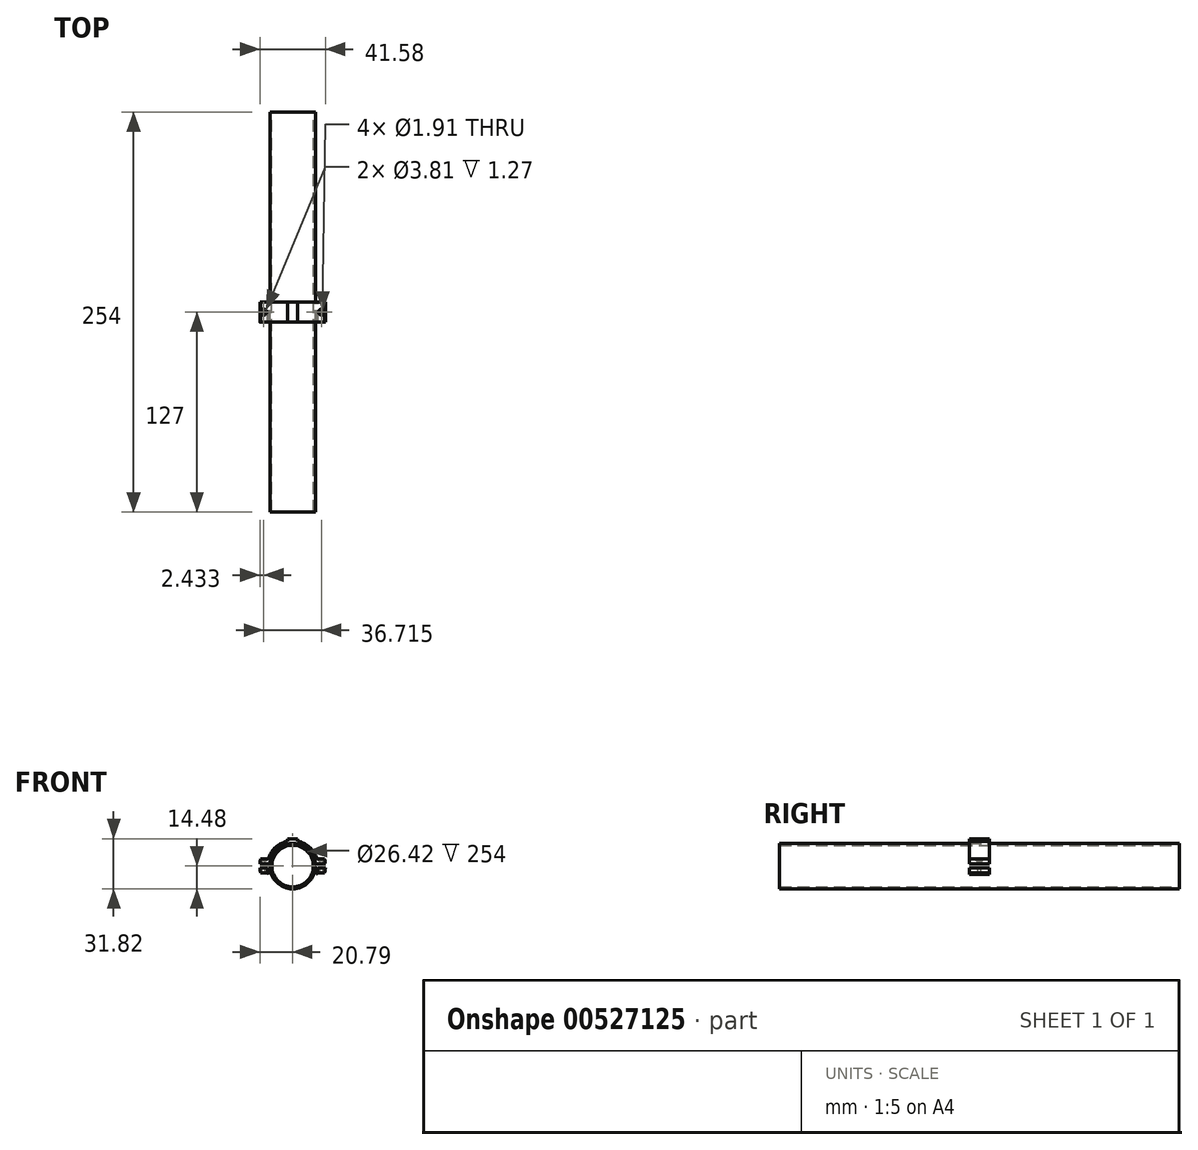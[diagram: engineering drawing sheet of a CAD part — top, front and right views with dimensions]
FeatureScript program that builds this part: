
annotation { "Feature Type Name" : "Feature", "Feature Type Description" : "" }
export const myFeature = defineFeature(function(context is Context, id is Id, definition is map)
    precondition{}
    {
        {
            var Q0;
            Q0=qCreatedBy(makeId("Front.planeOp"),FACE);
            var sketch = newSketch(context, id + "F0", { "sketchPlane" : qUnion([Q0])});
            skCircle(sketch, "E0", {"center": v(0, 0) * mm, "radius": 14.48 * mm});
            skCircle(sketch, "E1.0", {"center": v(0, 0) * mm, "radius": 13.2 * mm});
            skCircle(sketch, "E2", {"center": v(0, 0) * mm, "radius": 20.83 * mm});
            skCircle(sketch, "E3", {"center": v(0, 0) * mm, "radius": 16.07 * mm});
            skLineSegment(sketch, "E4.bottom", {"start": v(15.44, 4.45) * mm, "end": v(20.79, 4.45) * mm});
            skLineSegment(sketch, "E4.top", {"start": v(15.44, 1.27) * mm, "end": v(20.79, 1.27) * mm});
            skLineSegment(sketch, "E4.left", {"start": v(15.44, 4.45) * mm, "end": v(15.44, 1.27) * mm});
            skLineSegment(sketch, "E4.right", {"start": v(20.79, 4.45) * mm, "end": v(20.79, 1.27) * mm});
            skLineSegment(sketch, "E5", {"start": v(15.44, 1.27) * mm, "end": v(15.44, -4.45) * mm});
            skLineSegment(sketch, "E6.bottom", {"start": v(15.44, -4.45) * mm, "end": v(20.79, -4.45) * mm});
            skLineSegment(sketch, "E6.top", {"start": v(15.44, -1.27) * mm, "end": v(20.79, -1.27) * mm});
            skLineSegment(sketch, "E6.left", {"start": v(15.44, -4.45) * mm, "end": v(15.44, -1.27) * mm});
            skLineSegment(sketch, "E6.right", {"start": v(20.79, -4.45) * mm, "end": v(20.79, -1.27) * mm});
            skLineSegment(sketch, "E7.MirrorCS", {"start": v(-15.44, 4.45) * mm, "end": v(-20.79, 4.45) * mm});
            skLineSegment(sketch, "E8.MirrorCS", {"start": v(-20.79, 4.45) * mm, "end": v(-20.79, 1.27) * mm});
            skLineSegment(sketch, "E9.MirrorCS", {"start": v(-15.44, 1.27) * mm, "end": v(-20.79, 1.27) * mm});
            skLineSegment(sketch, "E10.MirrorCS", {"start": v(-15.44, 4.45) * mm, "end": v(-15.44, 1.27) * mm});
            skLineSegment(sketch, "E11.MirrorCS", {"start": v(-15.44, 1.27) * mm, "end": v(-15.44, -4.45) * mm});
            skLineSegment(sketch, "E12.MirrorCS", {"start": v(-15.44, -1.27) * mm, "end": v(-20.79, -1.27) * mm});
            skLineSegment(sketch, "E13.MirrorCS", {"start": v(-20.79, -4.45) * mm, "end": v(-20.79, -1.27) * mm});
            skLineSegment(sketch, "E14.MirrorCS", {"start": v(-15.44, -4.45) * mm, "end": v(-20.79, -4.45) * mm});
            skLineSegment(sketch, "E15.MirrorCS", {"start": v(-15.44, -4.45) * mm, "end": v(-15.44, -1.27) * mm});
            skLineSegment(sketch, "E16", {"start": v(-15.44, 1.27) * mm, "end": v(-14.42, 1.27) * mm});
            skLineSegment(sketch, "E17", {"start": v(-15.44, -1.27) * mm, "end": v(-14.42, -1.27) * mm});
            skLineSegment(sketch, "E18", {"start": v(15.44, 1.27) * mm, "end": v(14.42, 1.27) * mm});
            skCircle(sketch, "E19", {"center": v(16.37, -5.72) * mm, "radius": 1.27 * mm});
            skCircle(sketch, "E20", {"center": v(16.37, 5.72) * mm, "radius": 1.27 * mm});
            skCircle(sketch, "E21", {"center": v(-16.37, 5.72) * mm, "radius": 1.27 * mm});
            skCircle(sketch, "E22", {"center": v(-16.37, -5.72) * mm, "radius": 1.27 * mm});
            skLineSegment(sketch, "E23", {"start": v(15.44, -1.27) * mm, "end": v(14.42, -1.27) * mm});
            skLineSegment(sketch, "E24.bottom", {"start": v(-3.18, 17.34) * mm, "end": v(3.17, 17.34) * mm});
            skLineSegment(sketch, "E24.top", {"start": v(-3.18, 14.8) * mm, "end": v(3.17, 14.8) * mm});
            skLineSegment(sketch, "E24.left", {"start": v(-3.18, 17.34) * mm, "end": v(-3.18, 14.8) * mm});
            skLineSegment(sketch, "E24.right", {"start": v(3.18, 17.34) * mm, "end": v(3.17, 14.8) * mm});
            skPoint(sketch, "E24.middle", {"position": v(0, 16.07) * mm});
            skSolve(sketch);
        }
        {
            var Q0;
            Q0=makeQuery(id+"F0.imprint","IMPRINT",FACE,{"disambiguationData":[TD([[makeQuery(id+"F0.imprint","IMPRINT",EDGE,{"derivedFrom":sQuery(id+"F0.wireOp",EDGE,"E0")}),1.0]])]});
            extrude(context, id + "F1", {"entities" : qUnion([Q0]), "depth" : 254 * mm, "offsetDistance" : 25.4 * mm, "symmetric" : true});
        }
        {
            var Q0;
            {var subQ0=sQuery(id+"F0.wireOp",EDGE,"E7.MirrorCS");var subQ1=sQuery(id+"F0.wireOp",EDGE,"E2");var subQ2=makeQuery(id+"F0.imprint","INTERSECT",VERTEX,{"derivedFrom":[subQ1,subQ0]});Q0=makeQuery(id+"F0.imprint","IMPRINT",FACE,{"disambiguationData":[TD([[makeQuery(id+"F0.imprint","IMPRINT",EDGE,{"disambiguationData":[TD([[subQ2,1.0]])],"derivedFrom":subQ0}),1.0]])]});}
            var Q1;
            {var subQ0=sQuery(id+"F0.wireOp",EDGE,"E10.MirrorCS");Q1=makeQuery(id+"F0.imprint","IMPRINT",FACE,{"disambiguationData":[TD([[makeQuery(id+"F0.imprint","IMPRINT",EDGE,{"derivedFrom":subQ0}),-1.0]])]});}
            var Q2;
            {var subQ1=sQuery(id+"F0.wireOp",EDGE,"E3");var subQ3=sQuery(id+"F0.wireOp",EDGE,"E21");var subQ4=makeQuery(id+"F0.imprint","INTERSECT",VERTEX,{"derivedFrom":[subQ1,subQ3]});Q2=makeQuery(id+"F0.imprint","IMPRINT",FACE,{"disambiguationData":[TD([[makeQuery(id+"F0.imprint","IMPRINT",EDGE,{"disambiguationData":[TD([[subQ4,1.0]])],"derivedFrom":subQ3}),-1.0]])]});}
            var Q3;
            {var subQ3=sQuery(id+"F0.wireOp",EDGE,"E4.left");Q3=makeQuery(id+"F0.imprint","IMPRINT",FACE,{"disambiguationData":[TD([[makeQuery(id+"F0.imprint","IMPRINT",EDGE,{"derivedFrom":subQ3}),-1.0]])]});}
            var Q4;
            {var subQ0=sQuery(id+"F0.wireOp",EDGE,"E15.MirrorCS");Q4=makeQuery(id+"F0.imprint","IMPRINT",FACE,{"disambiguationData":[TD([[makeQuery(id+"F0.imprint","IMPRINT",EDGE,{"derivedFrom":subQ0}),1.0]])]});}
            var Q5;
            {var subQ0=sQuery(id+"F0.wireOp",EDGE,"E14.MirrorCS");var subQ5=sQuery(id+"F0.wireOp",EDGE,"E2");var subQ8=makeQuery(id+"F0.imprint","INTERSECT",VERTEX,{"derivedFrom":[subQ5,subQ0]});Q5=makeQuery(id+"F0.imprint","IMPRINT",FACE,{"disambiguationData":[TD([[makeQuery(id+"F0.imprint","IMPRINT",EDGE,{"disambiguationData":[TD([[subQ8,1.0]])],"derivedFrom":subQ0}),-1.0]])]});}
            var Q6;
            {var subQ1=sQuery(id+"F0.wireOp",EDGE,"E3");var subQ3=sQuery(id+"F0.wireOp",EDGE,"E22");var subQ4=makeQuery(id+"F0.imprint","INTERSECT",VERTEX,{"derivedFrom":[subQ1,subQ3]});Q6=makeQuery(id+"F0.imprint","IMPRINT",FACE,{"disambiguationData":[TD([[makeQuery(id+"F0.imprint","IMPRINT",EDGE,{"disambiguationData":[TD([[subQ4,-1.0]])],"derivedFrom":subQ3}),-1.0]])]});}
            var Q7;
            {var subQ1=sQuery(id+"F0.wireOp",EDGE,"E3");var subQ3=sQuery(id+"F0.wireOp",EDGE,"E19");var subQ4=makeQuery(id+"F0.imprint","INTERSECT",VERTEX,{"derivedFrom":[subQ1,subQ3]});Q7=makeQuery(id+"F0.imprint","IMPRINT",FACE,{"disambiguationData":[TD([[makeQuery(id+"F0.imprint","IMPRINT",EDGE,{"disambiguationData":[TD([[subQ4,1.0]])],"derivedFrom":subQ3}),-1.0]])]});}
            var Q8;
            {var subQ0=sQuery(id+"F0.wireOp",EDGE,"E6.left");Q8=makeQuery(id+"F0.imprint","IMPRINT",FACE,{"disambiguationData":[TD([[makeQuery(id+"F0.imprint","IMPRINT",EDGE,{"derivedFrom":subQ0}),-1.0]])]});}
            var Q9;
            {var subQ0=sQuery(id+"F0.wireOp",EDGE,"E6.bottom");var subQ1=sQuery(id+"F0.wireOp",EDGE,"E2");var subQ2=makeQuery(id+"F0.imprint","INTERSECT",VERTEX,{"derivedFrom":[subQ1,subQ0]});Q9=makeQuery(id+"F0.imprint","IMPRINT",FACE,{"disambiguationData":[TD([[makeQuery(id+"F0.imprint","IMPRINT",EDGE,{"disambiguationData":[TD([[subQ2,1.0]])],"derivedFrom":subQ0}),1.0]])]});}
            var Q10;
            {var subQ0=sQuery(id+"F0.wireOp",EDGE,"E4.left");Q10=makeQuery(id+"F0.imprint","IMPRINT",FACE,{"disambiguationData":[TD([[makeQuery(id+"F0.imprint","IMPRINT",EDGE,{"derivedFrom":subQ0}),1.0]])]});}
            var Q11;
            {var subQ0=sQuery(id+"F0.wireOp",EDGE,"E4.bottom");var subQ1=sQuery(id+"F0.wireOp",EDGE,"E2");var subQ2=makeQuery(id+"F0.imprint","INTERSECT",VERTEX,{"derivedFrom":[subQ1,subQ0]});Q11=makeQuery(id+"F0.imprint","IMPRINT",FACE,{"disambiguationData":[TD([[makeQuery(id+"F0.imprint","IMPRINT",EDGE,{"disambiguationData":[TD([[subQ2,1.0]])],"derivedFrom":subQ0}),-1.0]])]});}
            var Q12;
            {var subQ1=sQuery(id+"F0.wireOp",EDGE,"E3");var subQ3=sQuery(id+"F0.wireOp",EDGE,"E20");var subQ4=makeQuery(id+"F0.imprint","INTERSECT",VERTEX,{"derivedFrom":[subQ1,subQ3]});Q12=makeQuery(id+"F0.imprint","IMPRINT",FACE,{"disambiguationData":[TD([[makeQuery(id+"F0.imprint","IMPRINT",EDGE,{"disambiguationData":[TD([[subQ4,-1.0]])],"derivedFrom":subQ3}),-1.0]])]});}
            var Q13;
            {var subQ4=sQuery(id+"F0.wireOp",EDGE,"E6.left");Q13=makeQuery(id+"F0.imprint","IMPRINT",FACE,{"disambiguationData":[TD([[makeQuery(id+"F0.imprint","IMPRINT",EDGE,{"derivedFrom":subQ4}),1.0]])]});}
            var Q14;
            {var subQ5=sQuery(id+"F0.wireOp",EDGE,"E24.top");Q14=makeQuery(id+"F0.imprint","IMPRINT",FACE,{"disambiguationData":[TD([[makeQuery(id+"F0.imprint","IMPRINT",EDGE,{"derivedFrom":subQ5}),1.0]])]});}
            var Q15;
            {var subQ5=sQuery(id+"F0.wireOp",EDGE,"E24.bottom");Q15=makeQuery(id+"F0.imprint","IMPRINT",FACE,{"disambiguationData":[TD([[makeQuery(id+"F0.imprint","IMPRINT",EDGE,{"derivedFrom":subQ5}),-1.0]])]});}
            extrude(context, id + "F2", {"entities" : qUnion([Q0, Q1, Q2, Q3, Q4, Q5, Q6, Q7, Q8, Q9, Q10, Q11, Q12, Q13, Q14, Q15]), "depth" : 12.7 * mm, "offsetDistance" : 25.4 * mm, "symmetric" : true});
        }
        {
            var Q0;
            Q0=makeQuery(id+"F2.opExtrude","SWEPT_FACE",FACE,{"disambiguationData":[OSD([sQuery(id+"F0.wireOp",EDGE,"E4.bottom")])]});
            var sketch = newSketch(context, id + "F3", { "sketchPlane" : qUnion([Q0])});
            skCircle(sketch, "E25", {"center": v(18.36, 0) * mm, "radius": 1.9 * mm});
            skPoint(sketch, "E25.centerSnap0", {"position": v(18.36, -6.35) * mm});
            skPoint(sketch, "E25.centerSnap1", {"position": v(16.37, 0) * mm});
            skCircle(sketch, "E26", {"center": v(18.36, 0) * mm, "radius": 0.95 * mm});
            skSolve(sketch);
        }
        {
            var Q0;
            Q0=makeQuery(id+"F2.opExtrude","SWEPT_FACE",FACE,{"disambiguationData":[OSD([sQuery(id+"F0.wireOp",EDGE,"E7.MirrorCS")])]});
            var sketch = newSketch(context, id + "F4", { "sketchPlane" : qUnion([Q0])});
            skCircle(sketch, "E27", {"center": v(-18.36, 0) * mm, "radius": 1.9 * mm});
            skPoint(sketch, "E27.centerSnap0", {"position": v(-20.35, 0) * mm});
            skPoint(sketch, "E27.centerSnap1", {"position": v(-18.36, -6.35) * mm});
            skCircle(sketch, "E28", {"center": v(-18.36, 0) * mm, "radius": 0.95 * mm});
            skSolve(sketch);
        }
        {
            var Q0;
            Q0=makeQuery(id+"F3.imprint","IMPRINT",FACE,{"disambiguationData":[TD([[makeQuery(id+"F3.imprint","IMPRINT",EDGE,{"derivedFrom":sQuery(id+"F3.wireOp",EDGE,"E26")}),1.0]])]});
            var Q1;
            Q1=makeQuery(id+"F4.imprint","IMPRINT",FACE,{"disambiguationData":[TD([[makeQuery(id+"F4.imprint","IMPRINT",EDGE,{"derivedFrom":sQuery(id+"F4.wireOp",EDGE,"E28")}),1.0]])]});
            extrude(context, id + "F5", {"entities" : qUnion([Q0, Q1]), "operationType" : NewBodyOperationType.REMOVE, "oppositeDirection" : true, "depth" : 25.4 * mm, "offsetDistance" : 25.4 * mm});
        }
        {
            var Q0;
            Q0=makeQuery(id+"F3.imprint","IMPRINT",FACE,{"disambiguationData":[TD([[makeQuery(id+"F3.imprint","IMPRINT",EDGE,{"derivedFrom":sQuery(id+"F3.wireOp",EDGE,"E25")}),1.0]])]});
            var Q1;
            Q1=makeQuery(id+"F4.imprint","IMPRINT",FACE,{"disambiguationData":[TD([[makeQuery(id+"F4.imprint","IMPRINT",EDGE,{"derivedFrom":sQuery(id+"F4.wireOp",EDGE,"E27")}),1.0]])]});
            extrude(context, id + "F6", {"entities" : qUnion([Q0, Q1]), "operationType" : NewBodyOperationType.REMOVE, "oppositeDirection" : true, "depth" : 1.27 * mm, "offsetDistance" : 25.4 * mm});
        }
    });
